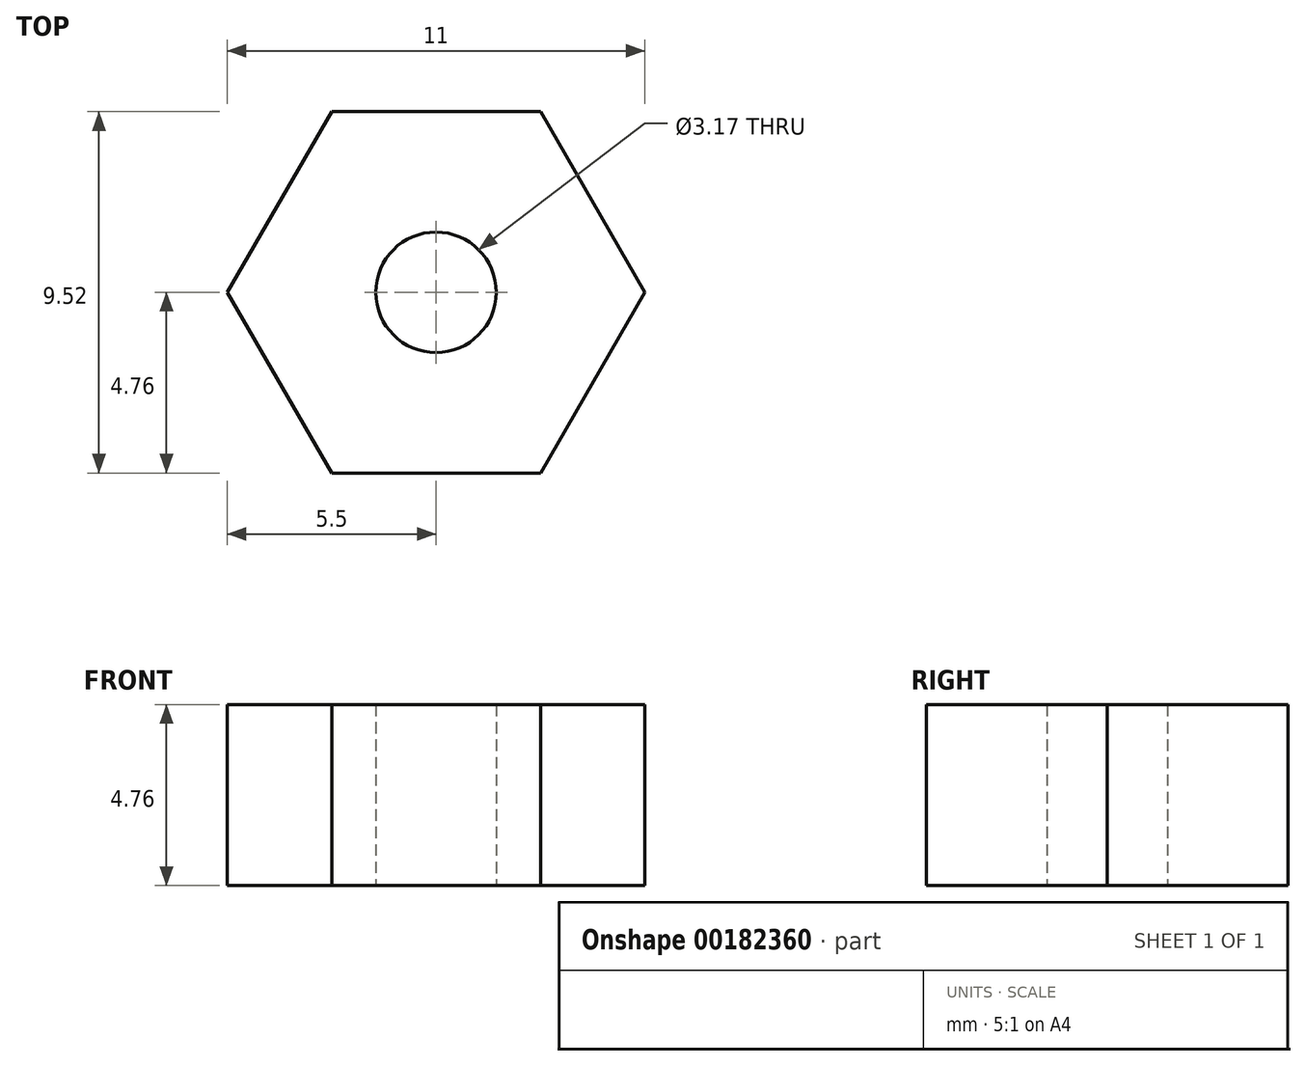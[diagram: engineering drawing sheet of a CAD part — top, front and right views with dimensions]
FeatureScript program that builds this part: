
annotation { "Feature Type Name" : "Feature", "Feature Type Description" : "" }
export const myFeature = defineFeature(function(context is Context, id is Id, definition is map)
    precondition{}
    {
        {
            var Q0;
            Q0=qCreatedBy(makeId("Top.planeOp"),FACE);
            var sketch = newSketch(context, id + "F0", { "sketchPlane" : qUnion([Q0])});
            skCircle(sketch, "E0.cCircle", {"center": v(0, 0) * mm, "radius": 4.76 * mm, "construction": true});
            skLineSegment(sketch, "E0.0", {"start": v(2.75, -4.76) * mm, "end": v(-2.75, -4.76) * mm});
            skLineSegment(sketch, "E0.1", {"start": v(-2.75, -4.76) * mm, "end": v(-5.5, 0) * mm});
            skLineSegment(sketch, "E0.2", {"start": v(-5.5, 0) * mm, "end": v(-2.75, 4.76) * mm});
            skLineSegment(sketch, "E0.3", {"start": v(-2.75, 4.76) * mm, "end": v(2.75, 4.76) * mm});
            skLineSegment(sketch, "E0.4", {"start": v(2.75, 4.76) * mm, "end": v(5.5, 0) * mm});
            skLineSegment(sketch, "E0.5", {"start": v(5.5, 0) * mm, "end": v(2.75, -4.76) * mm});
            skPoint(sketch, "E0.0.midPoint", {"position": v(0, -4.76) * mm});
            skCircle(sketch, "E1", {"center": v(0, 0) * mm, "radius": 1.59 * mm});
            skSolve(sketch);
        }
        {
            var Q0;
            Q0 = qSketchRegion(id + "F0", true);
            extrude(context, id + "F1", {"entities" : qUnion([Q0]), "depth" : 4.76 * mm});
        }
    });
